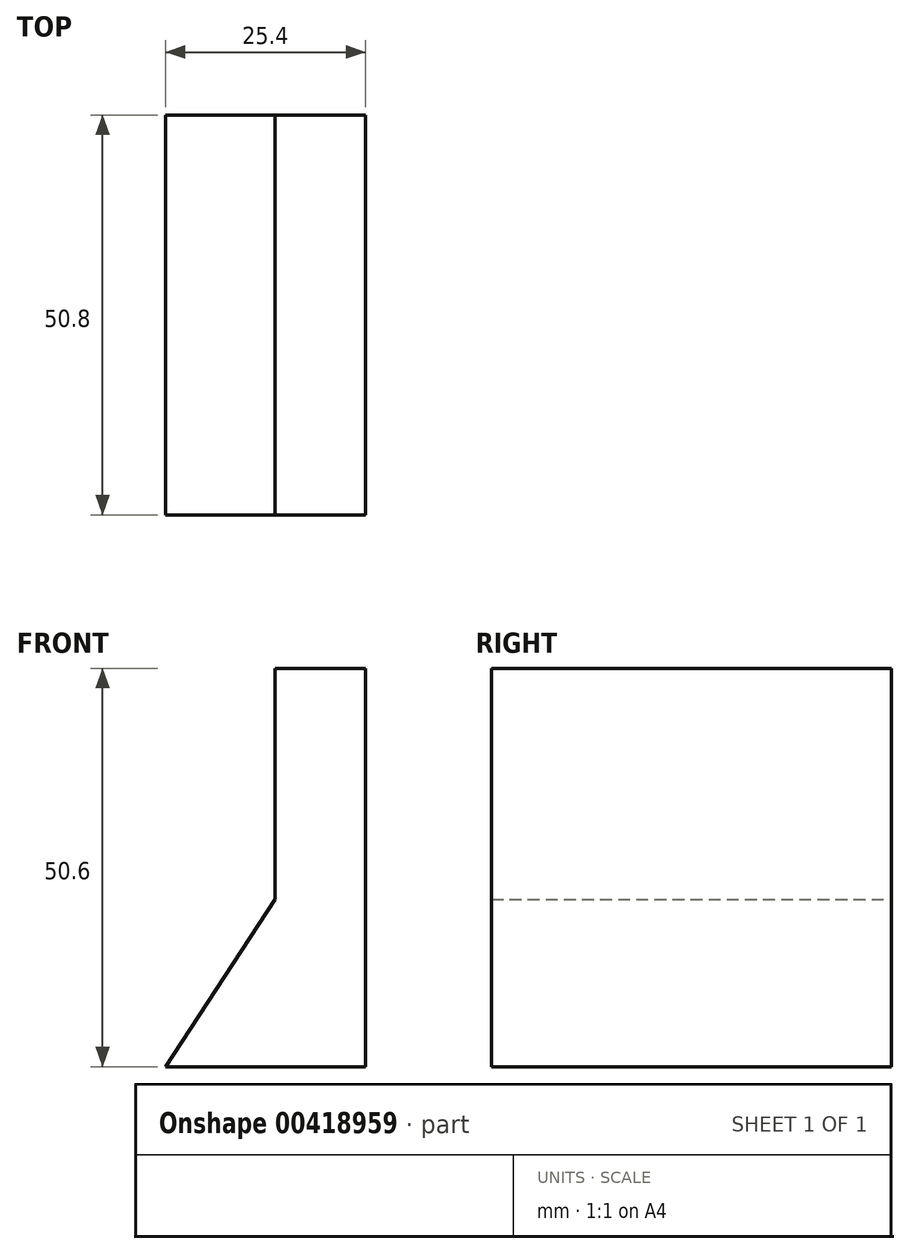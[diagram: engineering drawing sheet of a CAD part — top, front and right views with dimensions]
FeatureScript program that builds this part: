
annotation { "Feature Type Name" : "Feature", "Feature Type Description" : "" }
export const myFeature = defineFeature(function(context is Context, id is Id, definition is map)
    precondition{}
    {
        {
            var Q0;
            Q0=qCreatedBy(makeId("Front.planeOp"),FACE);
            var sketch = newSketch(context, id + "F0", { "sketchPlane" : qUnion([Q0])});
            skLineSegment(sketch, "E0", {"start": v(0, 50.8) * mm, "end": v(0, 0) * mm});
            skLineSegment(sketch, "E1", {"start": v(0, 0) * mm, "end": v(-25.4, 0) * mm});
            skLineSegment(sketch, "E2", {"start": v(-25.4, 0) * mm, "end": v(-11.5, 21.26) * mm});
            skLineSegment(sketch, "E3", {"start": v(-11.5, 21.26) * mm, "end": v(-11.5, 50.6) * mm});
            skLineSegment(sketch, "E4", {"start": v(-11.5, 50.6) * mm, "end": v(1.34, 50.6) * mm});
            skSolve(sketch);
        }
        {
            var Q0;
            Q0 = qSketchRegion(id + "F0", true);
            extrude(context, id + "F1", {"entities" : qUnion([Q0]), "depth" : 50.8 * mm});
        }
    });
